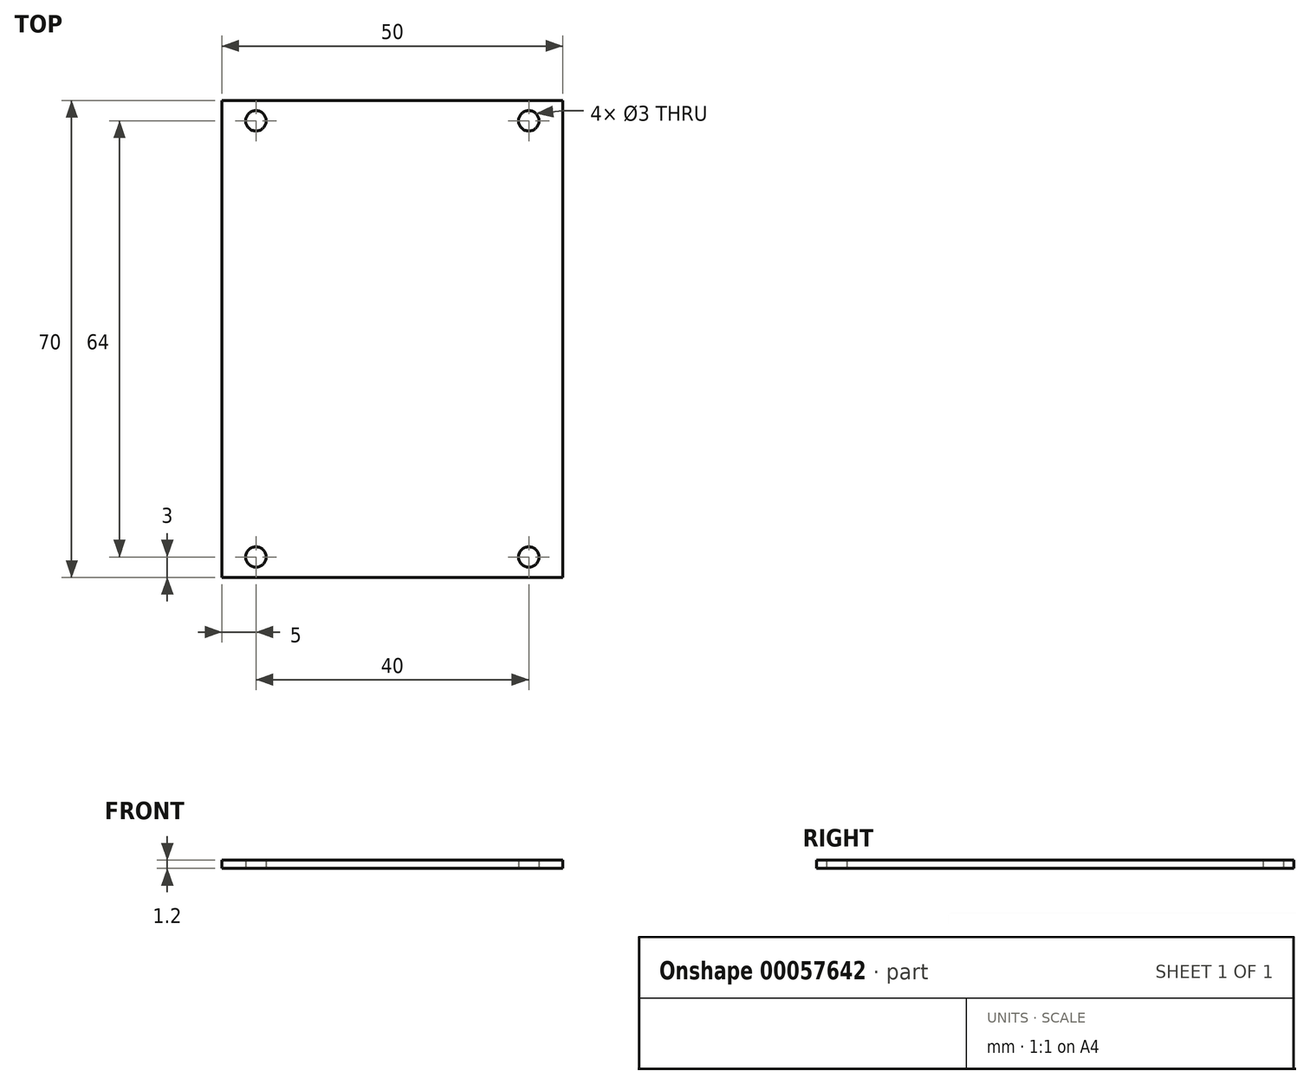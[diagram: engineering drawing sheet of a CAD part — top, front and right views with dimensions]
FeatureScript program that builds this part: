
annotation { "Feature Type Name" : "Feature", "Feature Type Description" : "" }
export const myFeature = defineFeature(function(context is Context, id is Id, definition is map)
    precondition{}
    {
        {
            var Q0;
            Q0=qCreatedBy(makeId("Top.planeOp"),FACE);
            var sketch = newSketch(context, id + "F0", { "sketchPlane" : qUnion([Q0])});
            skLineSegment(sketch, "E0.rect.bottom", {"start": v(25, -35) * mm, "end": v(-25, -35) * mm});
            skLineSegment(sketch, "E0.rect.top", {"start": v(25, 35) * mm, "end": v(-25, 35) * mm});
            skLineSegment(sketch, "E0.rect.left", {"start": v(25, -35) * mm, "end": v(25, 35) * mm});
            skLineSegment(sketch, "E0.rect.right", {"start": v(-25, -35) * mm, "end": v(-25, 35) * mm});
            skPoint(sketch, "E0.rect.middle", {"position": v(0, 0) * mm});
            skPoint(sketch, "E1", {"position": v(-20, 32) * mm});
            skPoint(sketch, "E2", {"position": v(20, 32) * mm});
            skPoint(sketch, "E3", {"position": v(-20, -32) * mm});
            skPoint(sketch, "E4", {"position": v(20, -32) * mm});
            skCircle(sketch, "E5", {"center": v(-20, 32) * mm, "radius": 1.5 * mm});
            skCircle(sketch, "E6", {"center": v(20, 32) * mm, "radius": 1.5 * mm});
            skCircle(sketch, "E7", {"center": v(20, -32) * mm, "radius": 1.5 * mm});
            skCircle(sketch, "E8", {"center": v(-20, -32) * mm, "radius": 1.5 * mm});
            skSolve(sketch);
        }
        {
            var Q0;
            Q0=makeQuery(id+"F0.imprint","IMPRINT",FACE,{"disambiguationData":[TD([[makeQuery(id+"F0.imprint","IMPRINT",EDGE,{"derivedFrom":sQuery(id+"F0.wireOp",EDGE,"E0.rect.bottom")}),-1.0]])]});
            extrude(context, id + "F1", {"entities" : qUnion([Q0]), "depth" : 1.2 * mm});
        }
    });
